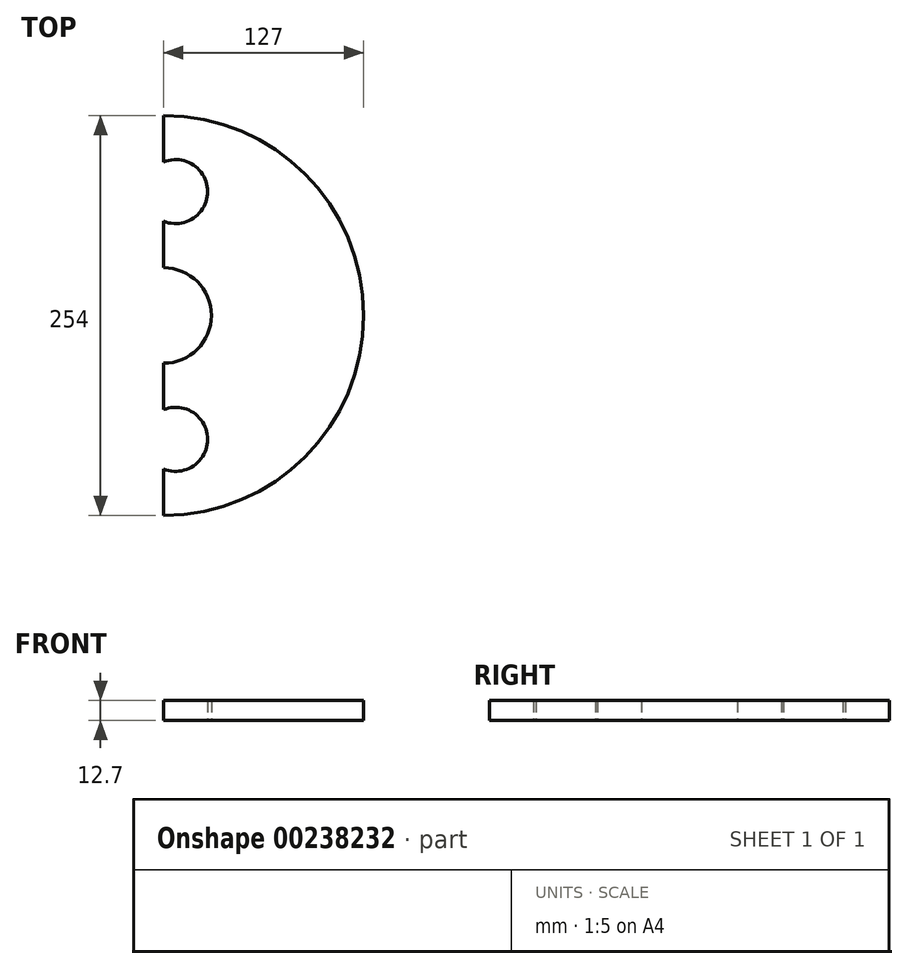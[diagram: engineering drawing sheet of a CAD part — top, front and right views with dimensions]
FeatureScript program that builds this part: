
annotation { "Feature Type Name" : "Feature", "Feature Type Description" : "" }
export const myFeature = defineFeature(function(context is Context, id is Id, definition is map)
    precondition{}
    {
        {
            var Q0;
            Q0=qCreatedBy(makeId("Top.planeOp"),FACE);
            var sketch = newSketch(context, id + "F0", { "sketchPlane" : qUnion([Q0])});
            skArc(sketch, "E0", {"start": v(309.75, 45.85) * mm, "mid": v(340.1, 76.2) * mm, "end": v(309.75, 106.55) * mm});
            skArc(sketch, "E1", {"start": v(309.75, -50.8) * mm, "mid": v(436.75, 76.2) * mm, "end": v(309.75, 203.2) * mm});
            skLineSegment(sketch, "E2", {"start": v(309.75, 106.55) * mm, "end": v(309.75, 136.04) * mm});
            skArc(sketch, "E3", {"start": v(309.75, 136.04) * mm, "mid": v(337.7, 154.88) * mm, "end": v(309.75, 173.71) * mm});
            skArc(sketch, "E4.MirrorC", {"start": v(309.75, 16.36) * mm, "mid": v(337.7, -2.48) * mm, "end": v(309.75, -21.31) * mm});
            skLineSegment(sketch, "E5.MirrorCS", {"start": v(309.75, 45.85) * mm, "end": v(309.75, 16.36) * mm});
            skLineSegment(sketch, "E6.trimOffspring", {"start": v(309.75, 173.71) * mm, "end": v(309.75, 203.2) * mm});
            skLineSegment(sketch, "E7.trimOffspring", {"start": v(309.75, -21.31) * mm, "end": v(309.75, -50.8) * mm});
            skSolve(sketch);
        }
        {
            var Q0;
            Q0=makeQuery(id+"F0.imprint","IMPRINT",FACE,{"disambiguationData":[TD([[makeQuery(id+"F0.imprint","IMPRINT",EDGE,{"derivedFrom":sQuery(id+"F0.wireOp",EDGE,"E0")}),-1.0]])]});
            extrude(context, id + "F1", {"entities" : qUnion([Q0]), "depth" : 12.7 * mm});
        }
    });
